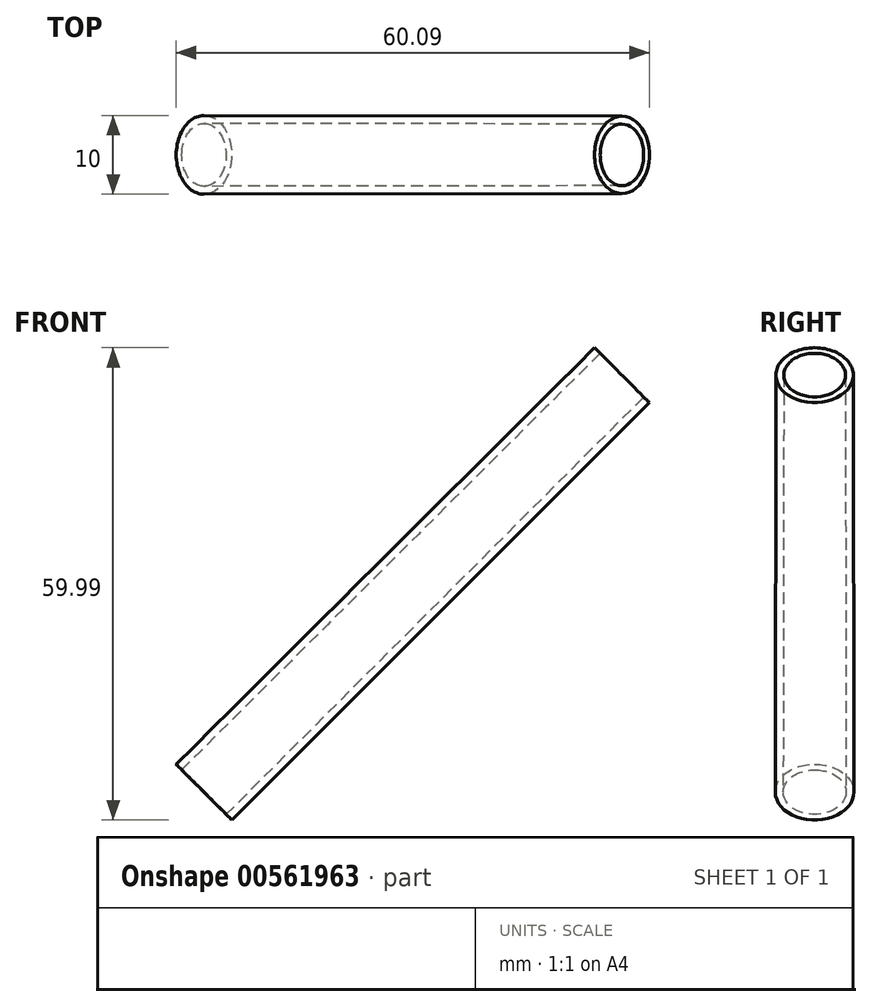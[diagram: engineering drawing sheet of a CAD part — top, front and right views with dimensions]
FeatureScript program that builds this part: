
annotation { "Feature Type Name" : "Feature", "Feature Type Description" : "" }
export const myFeature = defineFeature(function(context is Context, id is Id, definition is map)
    precondition{}
    {
        {
            var Q0;
            Q0=qCreatedBy(makeId("Front.planeOp"),FACE);
            var sketch = newSketch(context, id + "F0", { "sketchPlane" : qUnion([Q0])});
            skLineSegment(sketch, "E0", {"start": v(-44, -41.2) * mm, "end": v(9.03, 11.84) * mm});
            skLineSegment(sketch, "E1", {"start": v(9.03, 11.84) * mm, "end": v(9.73, 11.13) * mm});
            skLineSegment(sketch, "E2", {"start": v(9.73, 11.13) * mm, "end": v(-43.3, -41.9) * mm});
            skLineSegment(sketch, "E3", {"start": v(-43.3, -41.9) * mm, "end": v(-44, -41.2) * mm});
            skLineSegment(sketch, "E4", {"start": v(-46.9, -38.43) * mm, "end": v(5.7, 14.04) * mm, "construction": true});
            skSolve(sketch);
        }
        {
            var Q0;
            Q0=makeQuery(id+"F0.imprint","IMPRINT",FACE,{"disambiguationData":[TD([[makeQuery(id+"F0.imprint","IMPRINT",EDGE,{"derivedFrom":sQuery(id+"F0.wireOp",EDGE,"E0")}),-1.0]])]});
            var Q1;
            Q1=sQuery(id+"F0.wireOp",EDGE,"E4");
            revolve(context, id + "F1", {"entities" : qUnion([Q0]), "axis" : qUnion([Q1]), "revolveType" : RevolveType.FULL});
        }
    });
